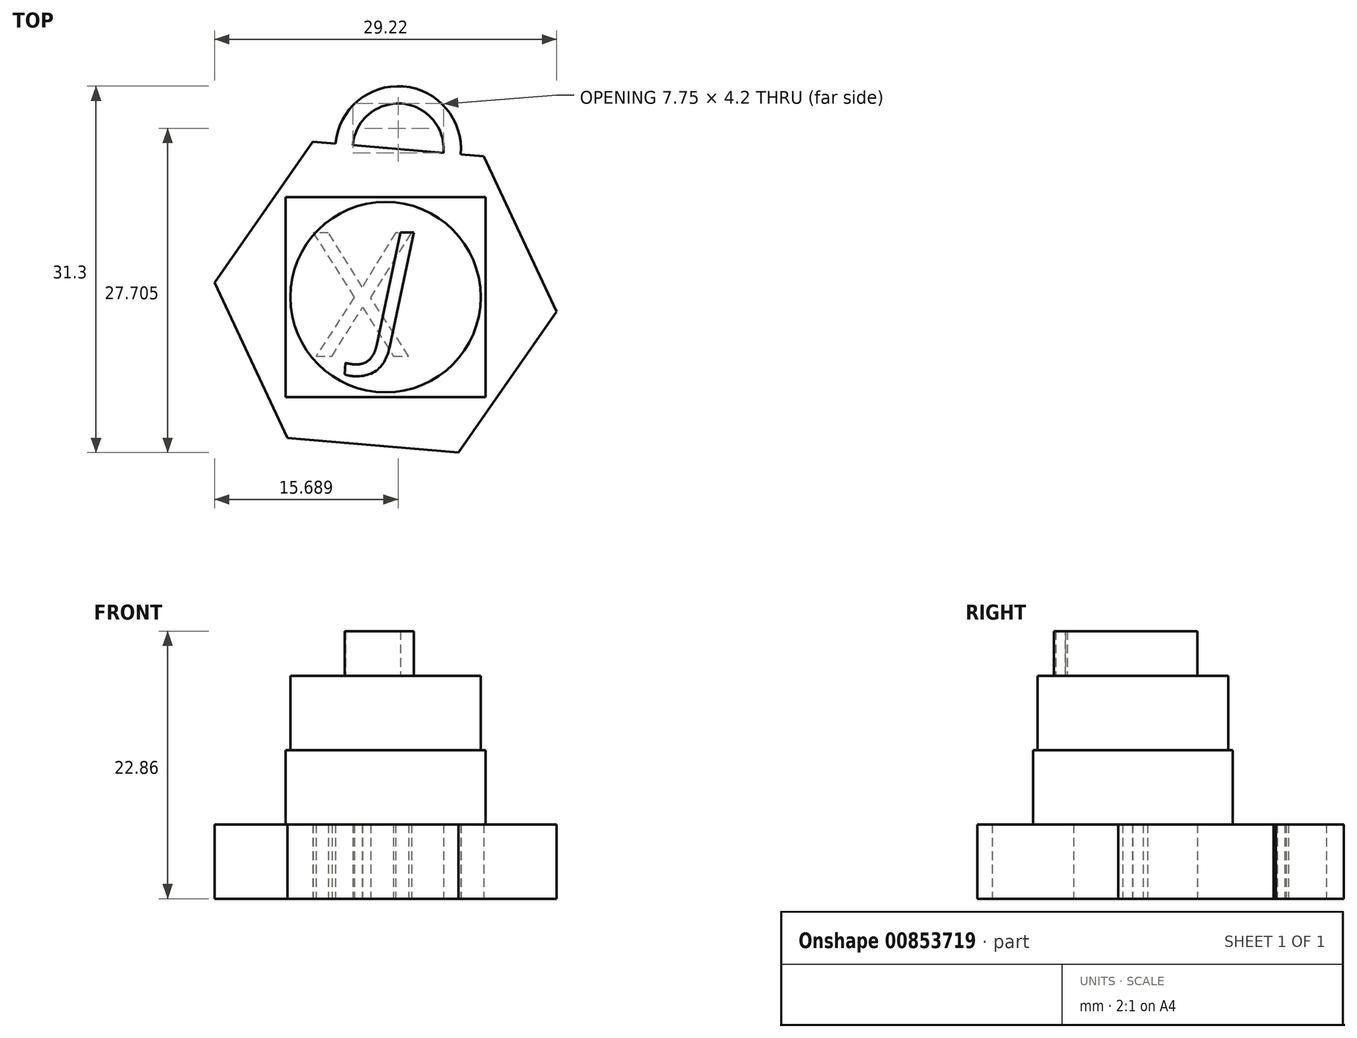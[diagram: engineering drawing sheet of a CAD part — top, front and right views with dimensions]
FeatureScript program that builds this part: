
annotation { "Feature Type Name" : "Feature", "Feature Type Description" : "" }
export const myFeature = defineFeature(function(context is Context, id is Id, definition is map)
    precondition{}
    {
        {
            var Q0;
            Q0=qCreatedBy(makeId("Top.planeOp"),FACE);
            var sketch = newSketch(context, id + "F0", { "sketchPlane" : qUnion([Q0])});
            skCircle(sketch, "E0.cCircle", {"center": v(0, 0) * mm, "radius": 12.7 * mm, "construction": true});
            skLineSegment(sketch, "E0.0", {"start": v(14.61, -1.25) * mm, "end": v(6.23, -13.28) * mm});
            skLineSegment(sketch, "E0.1", {"start": v(6.23, -13.28) * mm, "end": v(-8.39, -12.03) * mm});
            skLineSegment(sketch, "E0.2", {"start": v(-8.39, -12.03) * mm, "end": v(-14.61, 1.25) * mm});
            skLineSegment(sketch, "E0.3", {"start": v(-14.61, 1.25) * mm, "end": v(-6.23, 13.28) * mm});
            skLineSegment(sketch, "E0.4", {"start": v(-6.23, 13.28) * mm, "end": v(8.39, 12.03) * mm});
            skLineSegment(sketch, "E0.5", {"start": v(8.39, 12.03) * mm, "end": v(14.61, -1.25) * mm});
            skPoint(sketch, "E0.0.midPoint", {"position": v(10.42, -7.26) * mm});
            skSolve(sketch);
        }
        {
            var Q0;
            Q0=makeQuery(id+"F0.imprint","IMPRINT",FACE,{"disambiguationData":[TD([[makeQuery(id+"F0.imprint","IMPRINT",EDGE,{"derivedFrom":sQuery(id+"F0.wireOp",EDGE,"E0.0")}),-1.0]])]});
            extrude(context, id + "F1", {"entities" : qUnion([Q0]), "depth" : 6.35 * mm, "offsetDistance" : 25.4 * mm});
        }
        {
            var Q0;
            Q0=makeQuery(id+"F1.opExtrude","CAP_FACE",FACE,{"disambiguationData":[OSD([sQuery(id+"F0.wireOp",EDGE,"E0.0"),sQuery(id+"F0.wireOp",EDGE,"E0.1"),sQuery(id+"F0.wireOp",EDGE,"E0.2"),sQuery(id+"F0.wireOp",EDGE,"E0.3"),sQuery(id+"F0.wireOp",EDGE,"E0.4"),sQuery(id+"F0.wireOp",EDGE,"E0.5")])],"isStart":false});
            var sketch = newSketch(context, id + "F2", { "sketchPlane" : qUnion([Q0])});
            skCircle(sketch, "E1.cCircle", {"center": v(0, 0) * mm, "radius": 8.53 * mm, "construction": true});
            skPoint(sketch, "E1.cCircle.perimeterSnap0", {"position": v(10.42, -7.26) * mm});
            skLineSegment(sketch, "E1.0", {"start": v(8.53, -8.53) * mm, "end": v(-8.53, -8.53) * mm});
            skLineSegment(sketch, "E1.1", {"start": v(-8.53, -8.53) * mm, "end": v(-8.53, 8.53) * mm});
            skLineSegment(sketch, "E1.2", {"start": v(-8.53, 8.53) * mm, "end": v(8.53, 8.53) * mm});
            skLineSegment(sketch, "E1.3", {"start": v(8.53, 8.53) * mm, "end": v(8.53, -8.53) * mm});
            skPoint(sketch, "E1.0.midPoint.positionSnap0", {"position": v(10.42, -7.26) * mm});
            skSolve(sketch);
        }
        {
            var Q0;
            Q0=makeQuery(id+"F2.imprint","IMPRINT",FACE,{"disambiguationData":[TD([[makeQuery(id+"F2.imprint","IMPRINT",EDGE,{"derivedFrom":sQuery(id+"F2.wireOp",EDGE,"E1.0")}),1.0]])]});
            var sketch = newSketch(context, id + "F3", { "sketchPlane" : qUnion([Q0])});
            skCircle(sketch, "E2", {"center": v(0, 0) * mm, "radius": 8.13 * mm});
            skSolve(sketch);
        }
        {
            var Q0;
            Q0 = qSketchRegion(id + "F2", true);
            extrude(context, id + "F4", {"entities" : qUnion([Q0]), "operationType" : NewBodyOperationType.ADD, "depth" : 6.35 * mm, "offsetDistance" : 25.4 * mm});
        }
        {
            var Q0;
            Q0 = qSketchRegion(id + "F3", true);
            extrude(context, id + "F5", {"entities" : qUnion([Q0]), "operationType" : NewBodyOperationType.ADD, "depth" : 12.7 * mm, "offsetDistance" : 25.4 * mm});
        }
        {
            var Q0;
            Q0=makeQuery(id+"F5.opExtrude","CAP_FACE",FACE,{"disambiguationData":[OSD([sQuery(id+"F3.wireOp",EDGE,"E2")])],"isStart":false});
            var sketch = newSketch(context, id + "F6", { "sketchPlane" : qUnion([Q0])});
            skText(sketch, "E3", { "text": "J", "fontName": "OpenSans-Italic.ttf"});
            const initialGuessF6  = {"E3": [-0.00135, -0.0042, 1, 0, 0.0098]};
            skSetInitialGuess(sketch, initialGuessF6);
            skSolve(sketch);
        }
        {
            var Q0;
            Q0 = qSketchRegion(id + "F6", true);
            extrude(context, id + "F7", {"entities" : qUnion([Q0]), "operationType" : NewBodyOperationType.ADD, "depth" : 3.8 * mm, "offsetDistance" : 25.4 * mm});
        }
        {
            var Q0;
            Q0=makeQuery(id+"F1.opExtrude","CAP_FACE",FACE,{"disambiguationData":[OSD([sQuery(id+"F0.wireOp",EDGE,"E0.0"),sQuery(id+"F0.wireOp",EDGE,"E0.1"),sQuery(id+"F0.wireOp",EDGE,"E0.2"),sQuery(id+"F0.wireOp",EDGE,"E0.3"),sQuery(id+"F0.wireOp",EDGE,"E0.4"),sQuery(id+"F0.wireOp",EDGE,"E0.5")])],"isStart":true});
            var sketch = newSketch(context, id + "F8", { "sketchPlane" : qUnion([Q0])});
            skCircle(sketch, "E4", {"center": v(1.08, -12.65) * mm, "radius": 5.36 * mm});
            skCircle(sketch, "E5", {"center": v(1.08, -12.65) * mm, "radius": 3.89 * mm});
            skSolve(sketch);
        }
        {
            var Q0;
            {var subQ0=sQuery(id+"F8.wireOp",EDGE,"E4");var subQ1=makeQuery(id+"F1.opExtrude","CAP_EDGE",EDGE,{"disambiguationData":[OSD([sQuery(id+"F0.wireOp",EDGE,"E0.4")])],"isStart":true});var subQ2=makeQuery(id+"F8.imprint","INTERSECT",VERTEX,{"disambiguationData":[OD(0.0)],"derivedFrom":[subQ1,subQ0]});Q0=makeQuery(id+"F8.imprint","IMPRINT",FACE,{"disambiguationData":[TD([[makeQuery(id+"F8.imprint","IMPRINT",EDGE,{"disambiguationData":[TD([[subQ2,-1.0]])],"derivedFrom":subQ0}),1.0]])]});}
            extrude(context, id + "F9", {"entities" : qUnion([Q0]), "operationType" : NewBodyOperationType.ADD, "oppositeDirection" : true, "depth" : 6.35 * mm, "offsetDistance" : 25.4 * mm});
        }
        {
            var Q0;
            {var subQ0=sQuery(id+"F0.wireOp",EDGE,"E0.4");Q0=makeQuery(id+"F9.boolean.opBoolean","MERGE",FACE,{"derivedFrom":[makeQuery(id+"F1.opExtrude","CAP_FACE",FACE,{"disambiguationData":[OSD([sQuery(id+"F0.wireOp",EDGE,"E0.0"),sQuery(id+"F0.wireOp",EDGE,"E0.1"),sQuery(id+"F0.wireOp",EDGE,"E0.2"),sQuery(id+"F0.wireOp",EDGE,"E0.3"),subQ0,sQuery(id+"F0.wireOp",EDGE,"E0.5")])],"isStart":true}),makeQuery(id+"F9.opExtrude","CAP_FACE",FACE,{"disambiguationData":[OSD([subQ0,sQuery(id+"F8.wireOp",EDGE,"E4"),sQuery(id+"F8.wireOp",EDGE,"E5")])],"isStart":true})]});}
            var sketch = newSketch(context, id + "F10", { "sketchPlane" : qUnion([Q0])});
            skText(sketch, "E6", { "text": "X", "fontName": "OpenSans-Regular.ttf"});
            skPoint(sketch, "E6.firstSnap0", {"position": v(-11.5, 5.4) * mm});
            const initialGuessF10  = {"E6": [-0.00633, -0.00677, 1, 0, 0.01216]};
            skSetInitialGuess(sketch, initialGuessF10);
            skSolve(sketch);
        }
        {
            var Q0;
            Q0 = qSketchRegion(id + "F10", true);
            extrude(context, id + "F11", {"entities" : qUnion([Q0]), "operationType" : NewBodyOperationType.ADD, "depth" : -5.08 * mm, "offsetDistance" : 25.4 * mm});
        }
        {
            var Q0;
            {var subQ0=sQuery(id+"F0.wireOp",EDGE,"E0.4");Q0=makeQuery(id+"F9.boolean.opBoolean","MERGE",FACE,{"derivedFrom":[makeQuery(id+"F1.opExtrude","CAP_FACE",FACE,{"disambiguationData":[OSD([sQuery(id+"F0.wireOp",EDGE,"E0.0"),sQuery(id+"F0.wireOp",EDGE,"E0.1"),sQuery(id+"F0.wireOp",EDGE,"E0.2"),sQuery(id+"F0.wireOp",EDGE,"E0.3"),subQ0,sQuery(id+"F0.wireOp",EDGE,"E0.5")])],"isStart":true}),makeQuery(id+"F9.opExtrude","CAP_FACE",FACE,{"disambiguationData":[OSD([subQ0,sQuery(id+"F8.wireOp",EDGE,"E4"),sQuery(id+"F8.wireOp",EDGE,"E5")])],"isStart":true})]});}
            var sketch = newSketch(context, id + "F12", { "sketchPlane" : qUnion([Q0])});
            skText(sketch, "E7", { "text": "X", "fontName": "OpenSans-Regular.ttf"});
            const initialGuessF12  = {"E7": [-0.00623, -0.0055, 1, 0, 0.01064]};
            skSetInitialGuess(sketch, initialGuessF12);
            skSolve(sketch);
        }
        {
            var Q0;
            Q0 = qSketchRegion(id + "F12", true);
            extrude(context, id + "F13", {"entities" : qUnion([Q0]), "operationType" : NewBodyOperationType.REMOVE, "oppositeDirection" : true, "depth" : 6.35 * mm, "offsetDistance" : 25.4 * mm});
        }
    });
